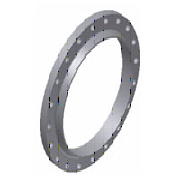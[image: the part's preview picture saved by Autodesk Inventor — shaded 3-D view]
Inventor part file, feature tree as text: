
AUTODESK INVENTOR PART (.ipt)
format: ipt  version: 2023.2 (Build 272271030, 271C)  size: 221,696 bytes
history: native  units: mm
features: other x5, pattern_circular x1, sketch x1
ambient origin geometry x8: Origin, YZ Plane, XZ Plane, XY Plane, X Axis, Y Axis, Z Axis, Center Point
bodies: Solid1 (feature_tree)
feature tree (7):
  pattern_circular  "Circular Pattern1"  Count=59  [1 undecoded]
  other  "Work Point1"
  other  "Work Point2"
  other  "Work Axis1"
  other  "Work Axis2"
  other  "Work Point3"
  sketch  "Sketch2"  dims[d2=457.0mm d3=400.0mm d4=454.0mm d5=424.0mm d6=95.0mm d7=50.0mm d8=6.0mm d13=7.0mm d14=90.0deg d15=33.0mm d16=265.0mm d20=10.0mm d21=0.0mm d22=200.0mm d23=360.0deg d25=4.0mm d26=4.0mm]
note: 1 required parameter value undecoded (feature->parameter linkage not recoverable at this tier; creation-order binding heuristic only, values carry confidence <= 0.55)
